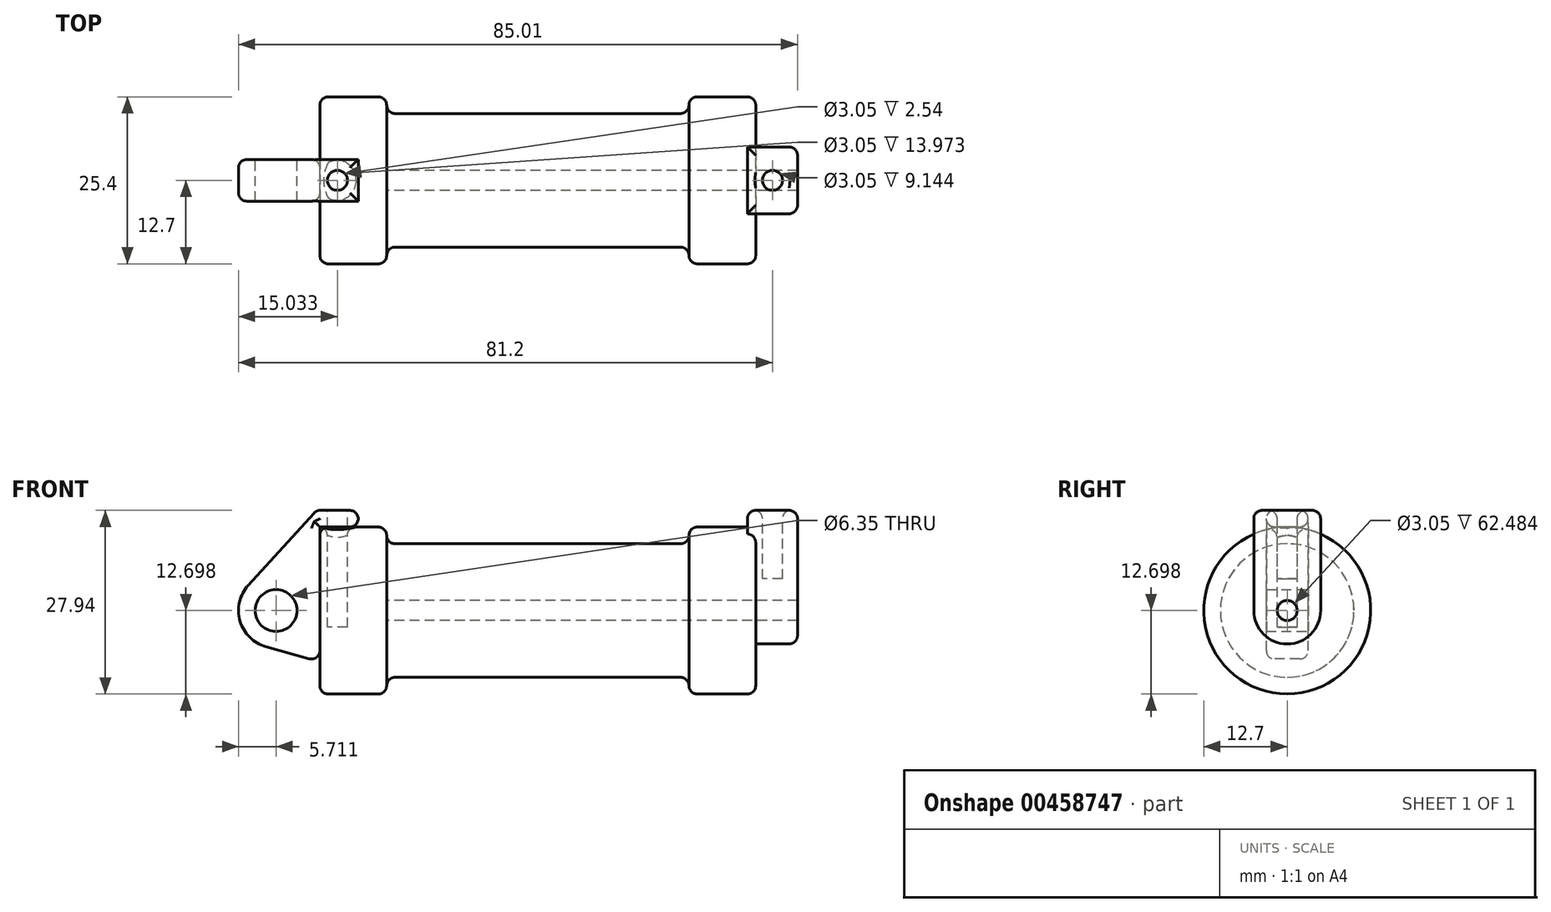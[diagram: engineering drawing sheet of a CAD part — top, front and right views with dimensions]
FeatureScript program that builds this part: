
annotation { "Feature Type Name" : "Feature", "Feature Type Description" : "" }
export const myFeature = defineFeature(function(context is Context, id is Id, definition is map)
    precondition{}
    {
        {
            var Q0;
            Q0=qCreatedBy(makeId("Front.planeOp"),FACE);
            var sketch = newSketch(context, id + "F0", { "sketchPlane" : qUnion([Q0])});
            skLineSegment(sketch, "E0", {"start": v(-16, -5.2) * mm, "end": v(-16, 7.5) * mm});
            skLineSegment(sketch, "E1", {"start": v(-16, 7.5) * mm, "end": v(-5.84, 7.5) * mm});
            skLineSegment(sketch, "E2", {"start": v(-5.84, 7.5) * mm, "end": v(-5.84, 4.97) * mm});
            skLineSegment(sketch, "E3", {"start": v(-5.84, 4.97) * mm, "end": v(40.13, 4.97) * mm});
            skLineSegment(sketch, "E4", {"start": v(40.13, 4.97) * mm, "end": v(40.13, 7.5) * mm});
            skLineSegment(sketch, "E5", {"start": v(40.13, 7.5) * mm, "end": v(50.3, 7.5) * mm});
            skLineSegment(sketch, "E6", {"start": v(50.3, 7.5) * mm, "end": v(50.3, -5.2) * mm});
            skLineSegment(sketch, "E7", {"start": v(50.3, -5.2) * mm, "end": v(-16, -5.2) * mm});
            skLineSegment(sketch, "E8", {"start": v(-10.16, 10.05) * mm, "end": v(-16.51, 10.05) * mm});
            skLineSegment(sketch, "E9", {"start": v(-16.51, 10.05) * mm, "end": v(-26.88, -1.34) * mm});
            skLineSegment(sketch, "E10", {"start": v(-16, -5.2) * mm, "end": v(-22.66, -5.2) * mm});
            skCircle(sketch, "E11", {"center": v(-22.66, -5.2) * mm, "radius": 5.72 * mm});
            skCircle(sketch, "E12", {"center": v(-22.66, -5.2) * mm, "radius": 3.18 * mm});
            skLineSegment(sketch, "E13", {"start": v(-10.16, 10.05) * mm, "end": v(-10.16, -14.6) * mm});
            skLineSegment(sketch, "E14", {"start": v(-10.16, -14.6) * mm, "end": v(-24.19, -10.7) * mm});
            skLineSegment(sketch, "E15", {"start": v(-16, -5.2) * mm, "end": v(-16, -12.97) * mm});
            skSolve(sketch);
        }
        {
            var Q0;
            {var subQ0=sQuery(id+"F0.wireOp",EDGE,"E2");Q0=makeQuery(id+"F0.imprint","IMPRINT",FACE,{"disambiguationData":[TD([[makeQuery(id+"F0.imprint","IMPRINT",EDGE,{"derivedFrom":subQ0}),-1.0]])]});}
            var Q1;
            {var subQ0=sQuery(id+"F0.wireOp",EDGE,"E0");Q1=makeQuery(id+"F0.imprint","IMPRINT",FACE,{"disambiguationData":[TD([[makeQuery(id+"F0.imprint","IMPRINT",EDGE,{"derivedFrom":subQ0}),-1.0]])]});}
            var Q2;
            Q2=sQuery(id+"F0.wireOp",EDGE,"E7");
            revolve(context, id + "F1", {"entities" : qUnion([Q0, Q1]), "axis" : qUnion([Q2]), "revolveType" : RevolveType.FULL});
        }
        {
            var Q0;
            {var subQ1=sQuery(id+"F0.wireOp",EDGE,"E0");Q0=makeQuery(id+"F0.imprint","IMPRINT",FACE,{"disambiguationData":[TD([[makeQuery(id+"F0.imprint","IMPRINT",EDGE,{"derivedFrom":subQ1}),1.0]])]});}
            var Q1;
            Q1=makeQuery(id+"F0.imprint","IMPRINT",FACE,{"disambiguationData":[TD([[makeQuery(id+"F0.imprint","IMPRINT",EDGE,{"derivedFrom":sQuery(id+"F0.wireOp",EDGE,"E12")}),-1.0]])]});
            var Q2;
            {var subQ0=sQuery(id+"F0.wireOp",EDGE,"E15");Q2=makeQuery(id+"F0.imprint","IMPRINT",FACE,{"disambiguationData":[TD([[makeQuery(id+"F0.imprint","IMPRINT",EDGE,{"derivedFrom":subQ0}),-1.0]])]});}
            extrude(context, id + "F2", {"entities" : qUnion([Q0, Q1, Q2]), "depth" : 6.35 * mm, "symmetric" : true});
        }
        {
            var Q0;
            Q0=makeQuery(id+"F1.opRevolve","SWEPT_FACE",FACE,{"disambiguationData":[OSD([sQuery(id+"F0.wireOp",EDGE,"E6")])]});
            var sketch = newSketch(context, id + "F3", { "sketchPlane" : qUnion([Q0])});
            skCircle(sketch, "E16", {"center": v(0, -5.2) * mm, "radius": 5.08 * mm});
            skCircle(sketch, "E17", {"center": v(0, -5.2) * mm, "radius": 1.52 * mm});
            skLineSegment(sketch, "E18", {"start": v(-5.08, -5.2) * mm, "end": v(-5.08, 10.05) * mm});
            skLineSegment(sketch, "E19", {"start": v(-5.08, 10.05) * mm, "end": v(5.08, 10.05) * mm});
            skLineSegment(sketch, "E20", {"start": v(5.08, 10.05) * mm, "end": v(5.08, -5.2) * mm});
            skSolve(sketch);
        }
        {
            var Q0;
            Q0 = qSketchRegion(id + "F3", true);
            extrude(context, id + "F4", {"entities" : qUnion([Q0]), "operationType" : NewBodyOperationType.ADD, "depth" : 6.35 * mm});
        }
        {
            var Q0;
            Q0 = qSketchRegion(id + "F3", true);
            extrude(context, id + "F5", {"entities" : qUnion([Q0]), "operationType" : NewBodyOperationType.ADD, "oppositeDirection" : true, "depth" : 1.27 * mm});
        }
        {
            var Q0;
            Q0=makeQuery(id+"F4.boolean.opBoolean","SPLIT",FACE,{"disambiguationData":[TD([makeQuery(id+"F4.opExtrude","SWEPT_FACE",FACE,{"disambiguationData":[OSD([sQuery(id+"F3.wireOp",EDGE,"E17")])]})])],"derivedFrom":makeQuery(id+"F1.opRevolve","SWEPT_FACE",FACE,{"disambiguationData":[OSD([sQuery(id+"F0.wireOp",EDGE,"E6")])]})});
            var Q1;
            Q1=makeQuery(id+"F1.opRevolve","SWEPT_FACE",FACE,{"disambiguationData":[OSD([sQuery(id+"F0.wireOp",EDGE,"E2")])]});
            extrude(context, id + "F6", {"entities" : qUnion([Q0]), "operationType" : NewBodyOperationType.REMOVE, "endBound" : BoundingType.UP_TO_SURFACE, "oppositeDirection" : true, "endBoundEntityFace" : qUnion([Q1]), "depth" : 25.4 * mm});
        }
        {
            var Q0;
            Q0=makeQuery(id+"F2.opExtrude","SWEPT_FACE",FACE,{"disambiguationData":[OSD([sQuery(id+"F0.wireOp",EDGE,"E8")])]});
            var sketch = newSketch(context, id + "F7", { "sketchPlane" : qUnion([Q0])});
            skCircle(sketch, "E21", {"center": v(-13.34, 0) * mm, "radius": 1.52 * mm});
            skCircle(sketch, "E22", {"center": v(52.83, 0) * mm, "radius": 1.52 * mm});
            skLineSegment(sketch, "E23.0", {"start": v(49.02, -5.08) * mm, "end": v(49.02, 5.08) * mm});
            skLineSegment(sketch, "E23.1", {"start": v(56.64, -5.08) * mm, "end": v(56.64, 5.08) * mm});
            skLineSegment(sketch, "E24.0", {"start": v(-16.51, -3.18) * mm, "end": v(-16.51, 3.17) * mm});
            skLineSegment(sketch, "E24.1", {"start": v(-10.16, -3.18) * mm, "end": v(-10.16, 3.17) * mm});
            skSolve(sketch);
        }
        {
            var Q0;
            Q0=makeQuery(id+"F7.imprint","IMPRINT",FACE,{"disambiguationData":[TD([[makeQuery(id+"F7.imprint","IMPRINT",EDGE,{"derivedFrom":sQuery(id+"F7.wireOp",EDGE,"E21")}),1.0]])]});
            extrude(context, id + "F8", {"entities" : qUnion([Q0]), "operationType" : NewBodyOperationType.REMOVE, "oppositeDirection" : true, "depth" : 17.78 * mm});
        }
        {
            var Q0;
            Q0=makeQuery(id+"F7.imprint","IMPRINT",FACE,{"disambiguationData":[TD([[makeQuery(id+"F7.imprint","IMPRINT",EDGE,{"derivedFrom":sQuery(id+"F7.wireOp",EDGE,"E22")}),1.0]])]});
            extrude(context, id + "F9", {"entities" : qUnion([Q0]), "operationType" : NewBodyOperationType.REMOVE, "oppositeDirection" : true, "depth" : 10.4 * mm});
        }
        {
            var Q0;
            Q0=makeQuery(id+"F2.opExtrude","CAP_EDGE",EDGE,{"disambiguationData":[OSD([sQuery(id+"F0.wireOp",EDGE,"E8")])],"isStart":false});
            var Q1;
            Q1=makeQuery(id+"F2.opExtrude","SWEPT_EDGE",EDGE,{"disambiguationData":[OSD([sQuery(id+"F0.wireOp",EDGE,"E8"),sQuery(id+"F0.wireOp",EDGE,"E9")])]});
            var Q2;
            Q2=makeQuery(id+"F2.opExtrude","CAP_EDGE",EDGE,{"disambiguationData":[OSD([sQuery(id+"F0.wireOp",EDGE,"E8")])],"isStart":true});
            var Q3;
            Q3=makeQuery(id+"F2.opExtrude","SWEPT_EDGE",EDGE,{"disambiguationData":[OSD([sQuery(id+"F0.wireOp",EDGE,"E8"),sQuery(id+"F0.wireOp",EDGE,"E13")])]});
            var Q4;
            Q4=makeQuery(id+"F2.opExtrude","SWEPT_FACE",FACE,{"disambiguationData":[OSD([sQuery(id+"F0.wireOp",EDGE,"E11")])]});
            var Q5;
            Q5=makeQuery(id+"F2.opExtrude","CAP_EDGE",EDGE,{"disambiguationData":[OSD([sQuery(id+"F0.wireOp",EDGE,"E0"),sQuery(id+"F0.wireOp",EDGE,"E15")])],"isStart":true});
            var Q6;
            Q6=makeQuery(id+"F2.opExtrude","SWEPT_EDGE",EDGE,{"disambiguationData":[OSD([sQuery(id+"F0.wireOp",EDGE,"E14"),sQuery(id+"F0.wireOp",EDGE,"E15")])]});
            var Q7;
            Q7=makeQuery(id+"F2.opExtrude","CAP_EDGE",EDGE,{"disambiguationData":[OSD([sQuery(id+"F0.wireOp",EDGE,"E0"),sQuery(id+"F0.wireOp",EDGE,"E15")])],"isStart":false});
            var Q8;
            Q8=makeQuery(id+"F2.opExtrude","SWEPT_EDGE",EDGE,{"disambiguationData":[OSD([sQuery(id+"F0.wireOp",EDGE,"E1"),sQuery(id+"F0.wireOp",EDGE,"E13")])]});
            var Q9;
            Q9=makeQuery(id+"F2.opExtrude","CAP_EDGE",EDGE,{"disambiguationData":[OSD([sQuery(id+"F0.wireOp",EDGE,"E1")])],"isStart":false});
            var Q10;
            Q10=makeQuery(id+"F2.opExtrude","CAP_EDGE",EDGE,{"disambiguationData":[OSD([sQuery(id+"F0.wireOp",EDGE,"E1")])],"isStart":true});
            var Q11;
            Q11=makeQuery(id+"F1.opRevolve","SWEPT_FACE",FACE,{"disambiguationData":[OSD([sQuery(id+"F0.wireOp",EDGE,"E1")])]});
            var Q12;
            Q12=makeQuery(id+"F1.opRevolve","SWEPT_EDGE",EDGE,{"disambiguationData":[OSD([sQuery(id+"F0.wireOp",EDGE,"E2"),sQuery(id+"F0.wireOp",EDGE,"E3")])]});
            var Q13;
            {var subQ0=sQuery(id+"F0.wireOp",EDGE,"E5");var subQ1=sQuery(id+"F0.wireOp",EDGE,"E6");Q13=makeQuery(id+"F4.boolean.opBoolean","SPLIT",EDGE,{"disambiguationData":[topologyDisambiguationEdgeConnected([makeQuery(id+"F1.opRevolve","SWEPT_FACE",FACE,{"disambiguationData":[OSD([subQ1])]})])],"derivedFrom":makeQuery(id+"F1.opRevolve","SWEPT_EDGE",EDGE,{"disambiguationData":[OSD([subQ0,subQ1])]})});}
            var Q14;
            Q14=makeQuery(id+"F1.opRevolve","SWEPT_EDGE",EDGE,{"disambiguationData":[OSD([sQuery(id+"F0.wireOp",EDGE,"E4"),sQuery(id+"F0.wireOp",EDGE,"E5")])]});
            var Q15;
            Q15=makeQuery(id+"F1.opRevolve","SWEPT_EDGE",EDGE,{"disambiguationData":[OSD([sQuery(id+"F0.wireOp",EDGE,"E3"),sQuery(id+"F0.wireOp",EDGE,"E4")])]});
            var Q16;
            Q16=makeQuery(id+"F4.opExtrude","CAP_EDGE",EDGE,{"disambiguationData":[OSD([sQuery(id+"F3.wireOp",EDGE,"E20")])],"isStart":false});
            var Q17;
            Q17=makeQuery(id+"F4.opExtrude","CAP_EDGE",EDGE,{"disambiguationData":[OSD([sQuery(id+"F3.wireOp",EDGE,"E19")])],"isStart":false});
            var Q18;
            Q18=makeQuery(id+"F4.opExtrude","CAP_EDGE",EDGE,{"disambiguationData":[OSD([sQuery(id+"F3.wireOp",EDGE,"E16")])],"isStart":true});
            var Q19;
            {var subQ0=sQuery(id+"F3.wireOp",EDGE,"E19");Q19=makeQuery(id+"F5.boolean.opBoolean","MERGE",FACE,{"derivedFrom":[makeQuery(id+"F4.opExtrude","SWEPT_FACE",FACE,{"disambiguationData":[OSD([subQ0])]}),makeQuery(id+"F5.opExtrude","SWEPT_FACE",FACE,{"disambiguationData":[OSD([subQ0])]})]});}
            fillet(context, id + "F10", {"entities" : qUnion([Q0, Q1, Q2, Q3, Q4, Q5, Q6, Q7, Q8, Q9, Q10, Q11, Q12, Q13, Q14, Q15, Q16, Q17, Q18, Q19]), "radius" : 1.27 * mm, "tangentPropagation" : true, "allowEdgeOverflow" : false});
        }
    });
